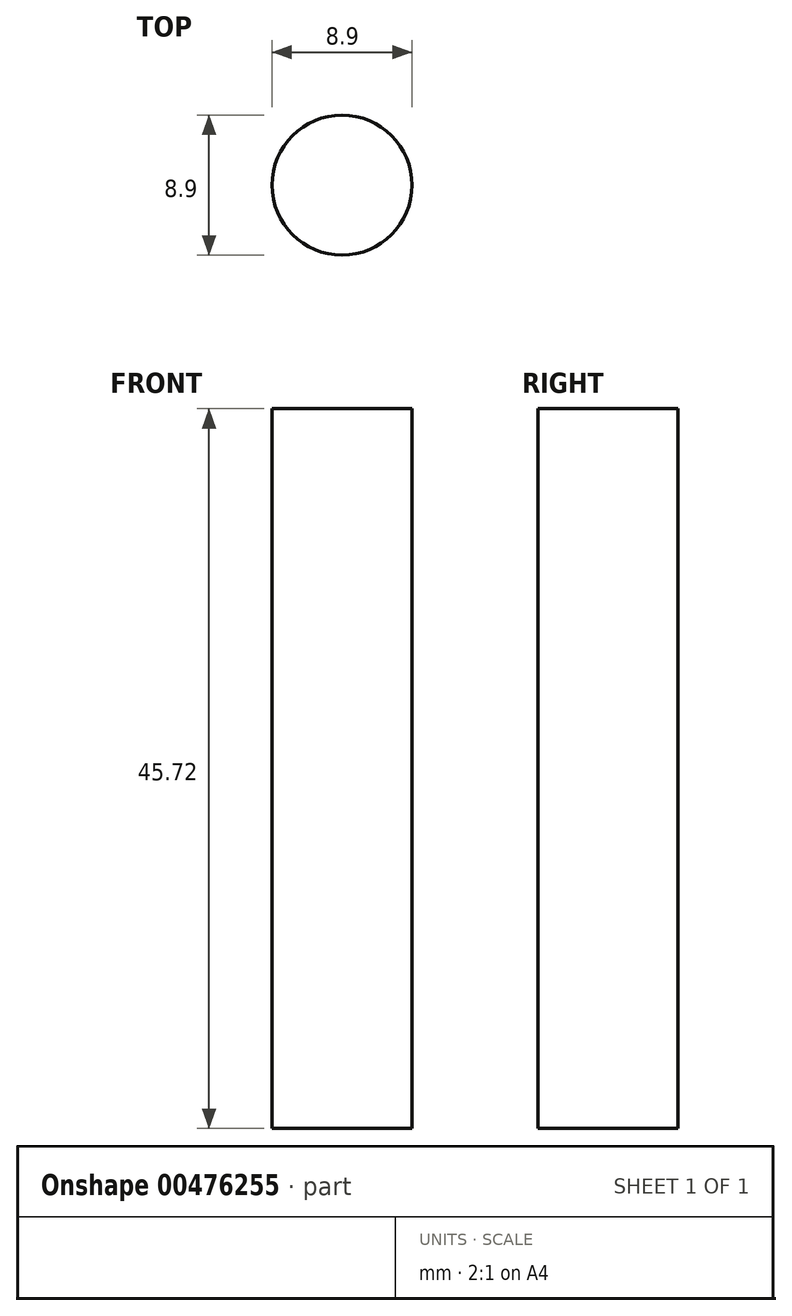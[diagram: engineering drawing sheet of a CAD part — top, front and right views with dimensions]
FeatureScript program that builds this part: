
annotation { "Feature Type Name" : "Feature", "Feature Type Description" : "" }
export const myFeature = defineFeature(function(context is Context, id is Id, definition is map)
    precondition{}
    {
        {
            var Q0;
            Q0=qCreatedBy(makeId("Top.planeOp"),FACE);
            var sketch = newSketch(context, id + "F0", { "sketchPlane" : qUnion([Q0])});
            skCircle(sketch, "E0", {"center": v(0, 0) * mm, "radius": 4.45 * mm});
            skSolve(sketch);
        }
        {
            var Q0;
            Q0 = qSketchRegion(id + "F0", true);
            extrude(context, id + "F1", {"entities" : qUnion([Q0]), "depth" : 45.72 * mm});
        }
    });
